# Revit family: Single Handle Lavatory Faucet with pop-up waste_TOTO_TLG08301
name_source: partatom
category: 衛生器具
revit_build: Autodesk Revit 2018 (Build: 20170223_1515(x64)
units: mm (PartAtom-declared; Revit-internal decimal feet)

## family parameters
OmniClass タイトル = Sanitary, Laundry, and Cleaning Equipment
OmniClass 番号 = 23.45.00.00
パーツ タイプ = 標準
ロード時にボイドで切り取り = いいえ
丸型コネクタ寸法 = 直径を使用
作業面ベース = いいえ
共有 = いいえ
常に垂直 = はい
部屋計算ポイント = いいえ

## types (1)
- Single Handle Lavatory Faucet with pop-up waste_TOTO_TLG08301
    Chrome = Chrome
    Height = 160  [stored 0.524934 ft]
    Length = 155
    TOTO asiaoceania = TLG08301V
    TOTO china = TLG08301B
    TOTO europe = TLG08301E
    TOTO hongkong = TLG08301H
    TOTO india = TLG08301B
    TOTO korea = TLG08301K
    TOTO russia = TLG08301R
    TOTO taiwan = TLG08301P
    TOTO thailand = TLG08301T
    TOTO usa = TLG08301U
    TOTO vietnam = TLG08301V
    Width = 65
    製造元 = TOTO LTD.
    説明 = Single Handle Lavatory Faucet with pop-up waste

note: [stored X ft] marks values corroborated as IEEE doubles in the binary element streams (Revit-internal decimal feet)
